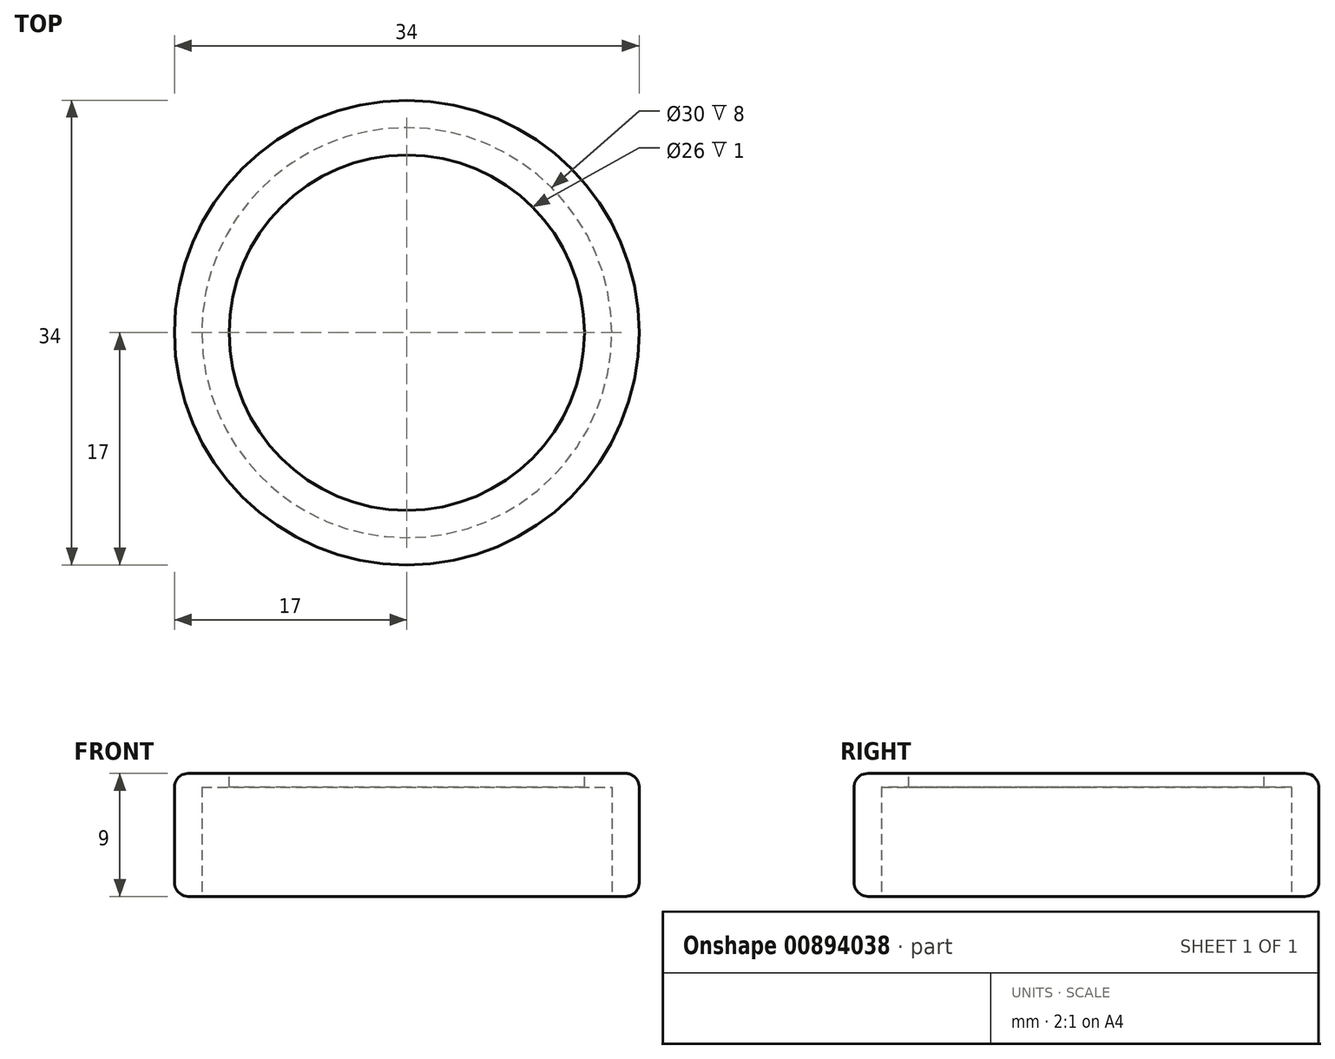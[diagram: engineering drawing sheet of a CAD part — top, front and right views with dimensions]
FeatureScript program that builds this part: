
annotation { "Feature Type Name" : "Feature", "Feature Type Description" : "" }
export const myFeature = defineFeature(function(context is Context, id is Id, definition is map)
    precondition{}
    {
        {
            var Q0;
            Q0=qCreatedBy(makeId("Top.planeOp"),FACE);
            var sketch = newSketch(context, id + "F0", { "sketchPlane" : qUnion([Q0])});
            skCircle(sketch, "E0", {"center": v(0, 0) * mm, "radius": 17 * mm});
            skSolve(sketch);
        }
        {
            var Q0;
            Q0 = qSketchRegion(id + "F0", true);
            extrude(context, id + "F1", {"entities" : qUnion([Q0]), "depth" : 8 * mm, "offsetDistance" : 25 * mm});
        }
        {
            var Q0;
            Q0=makeQuery(id+"F1.opExtrude","CAP_FACE",FACE,{"disambiguationData":[OSD([sQuery(id+"F0.wireOp",EDGE,"E0")])],"isStart":true});
            var sketch = newSketch(context, id + "F2", { "sketchPlane" : qUnion([Q0])});
            skCircle(sketch, "E1", {"center": v(0, 0) * mm, "radius": 15 * mm});
            skSolve(sketch);
        }
        {
            var Q0;
            Q0=makeQuery(id+"F2.imprint","IMPRINT",FACE,{"disambiguationData":[TD([[makeQuery(id+"F2.imprint","IMPRINT",EDGE,{"derivedFrom":sQuery(id+"F2.wireOp",EDGE,"E1")}),1.0]])]});
            extrude(context, id + "F3", {"entities" : qUnion([Q0]), "operationType" : NewBodyOperationType.REMOVE, "oppositeDirection" : true, "depth" : 8 * mm, "offsetDistance" : 25 * mm});
        }
        {
            var Q0;
            Q0=makeQuery(id+"F1.opExtrude","CAP_FACE",FACE,{"disambiguationData":[OSD([sQuery(id+"F0.wireOp",EDGE,"E0")])],"isStart":false});
            var sketch = newSketch(context, id + "F4", { "sketchPlane" : qUnion([Q0])});
            skCircle(sketch, "E2", {"center": v(0, 0) * mm, "radius": 17 * mm});
            skSolve(sketch);
        }
        {
            var Q0;
            Q0 = qSketchRegion(id + "F4", true);
            extrude(context, id + "F5", {"entities" : qUnion([Q0]), "operationType" : NewBodyOperationType.ADD, "depth" : 1 * mm, "offsetDistance" : 25 * mm});
        }
        {
            var Q0;
            Q0=makeQuery(id+"F5.opExtrude","CAP_FACE",FACE,{"disambiguationData":[OSD([sQuery(id+"F4.wireOp",EDGE,"E2")])],"isStart":false});
            var sketch = newSketch(context, id + "F6", { "sketchPlane" : qUnion([Q0])});
            skCircle(sketch, "E3", {"center": v(0, 0) * mm, "radius": 13 * mm});
            skSolve(sketch);
        }
        {
            var Q0;
            Q0 = qSketchRegion(id + "F6", true);
            extrude(context, id + "F7", {"entities" : qUnion([Q0]), "operationType" : NewBodyOperationType.REMOVE, "oppositeDirection" : true, "depth" : 1 * mm, "offsetDistance" : 25 * mm});
        }
        {
            var Q0;
            Q0=makeQuery(id+"F1.opExtrude","CAP_EDGE",EDGE,{"disambiguationData":[OSD([sQuery(id+"F0.wireOp",EDGE,"E0")])],"isStart":true});
            var Q1;
            Q1=makeQuery(id+"F3.boolean.opBoolean","COPY",EDGE,{"derivedFrom":makeQuery(id+"F3.opExtrude","CAP_EDGE",EDGE,{"disambiguationData":[OSD([sQuery(id+"F2.wireOp",EDGE,"E1")])],"isStart":true})});
            fillet(context, id + "F8", {"entities" : qUnion([Q0, Q1]), "radius" : 1 * mm, "tangentPropagation" : true, "allowEdgeOverflow" : false});
        }
        {
            var Q0;
            Q0=makeQuery(id+"F5.opExtrude","CAP_EDGE",EDGE,{"disambiguationData":[OSD([sQuery(id+"F4.wireOp",EDGE,"E2")])],"isStart":false});
            fillet(context, id + "F9", {"entities" : qUnion([Q0]), "radius" : 1 * mm, "tangentPropagation" : true, "allowEdgeOverflow" : false});
        }
    });
